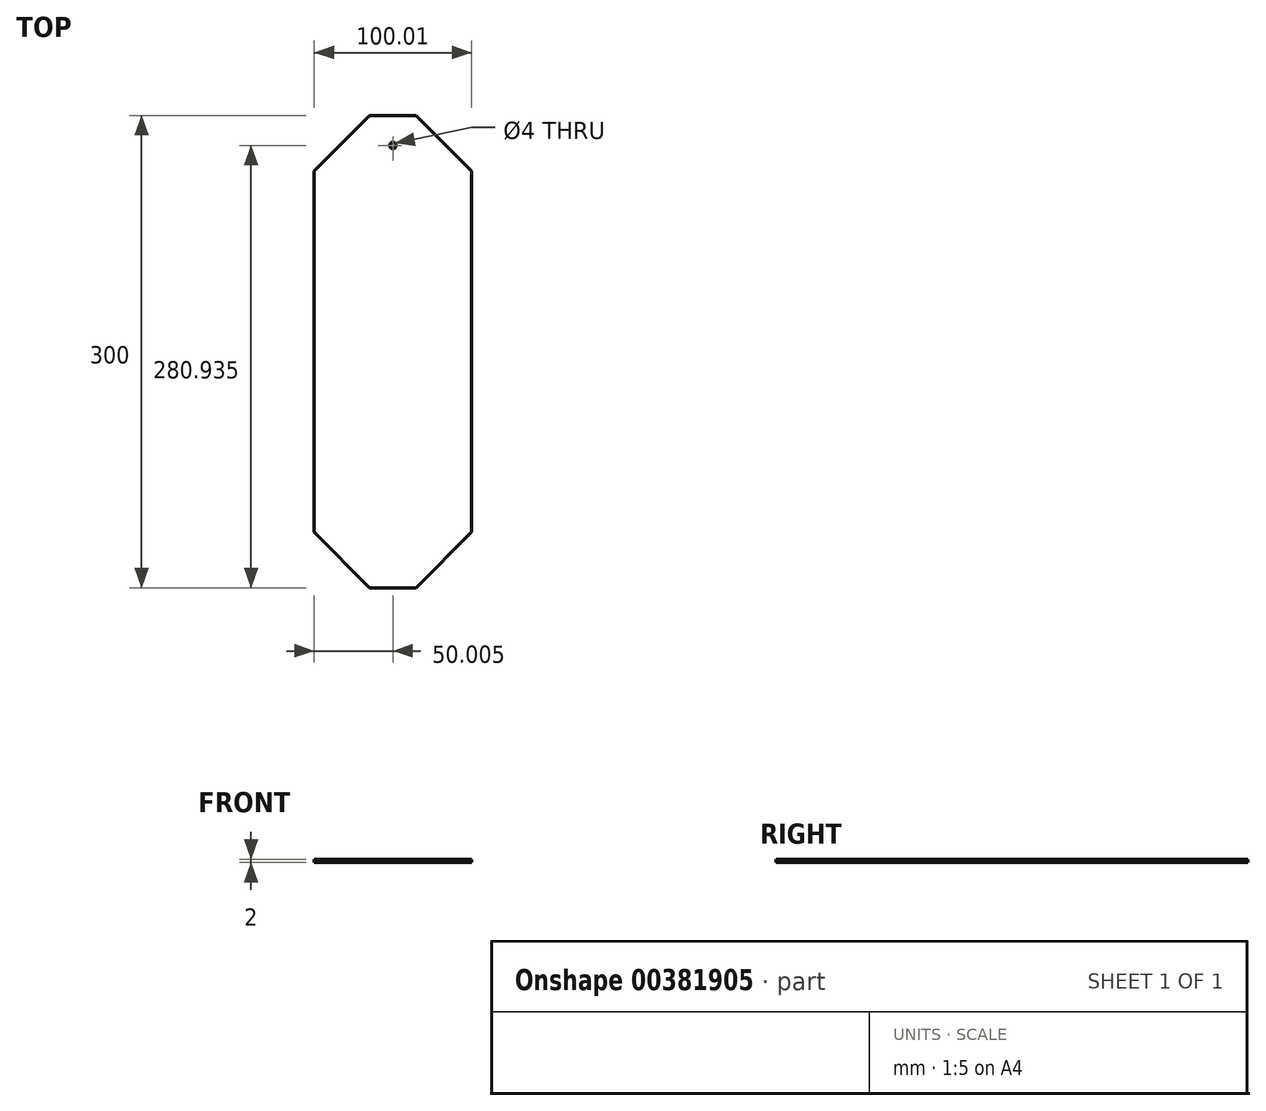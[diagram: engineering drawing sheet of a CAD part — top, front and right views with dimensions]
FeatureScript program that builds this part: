
annotation { "Feature Type Name" : "Feature", "Feature Type Description" : "" }
export const myFeature = defineFeature(function(context is Context, id is Id, definition is map)
    precondition{}
    {
        {
            var Q0;
            Q0=qCreatedBy(makeId("Top.planeOp"),FACE);
            var sketch = newSketch(context, id + "F0", { "sketchPlane" : qUnion([Q0])});
            skLineSegment(sketch, "E0", {"start": v(0, 0) * mm, "end": v(29.3, 0) * mm});
            skLineSegment(sketch, "E1", {"start": v(0, 0) * mm, "end": v(-35.35, 35.36) * mm});
            skLineSegment(sketch, "E2", {"start": v(-35.35, 35.36) * mm, "end": v(-35.35, 264.64) * mm});
            skLineSegment(sketch, "E3", {"start": v(-35.36, 264.64) * mm, "end": v(0, 300) * mm});
            skLineSegment(sketch, "E4", {"start": v(0, 300) * mm, "end": v(29.29, 300) * mm});
            skLineSegment(sketch, "E5", {"start": v(14.64, 300) * mm, "end": v(14.65, 0) * mm, "construction": true});
            skLineSegment(sketch, "E6.MirrorCS", {"start": v(64.65, 264.64) * mm, "end": v(29.3, 300) * mm});
            skLineSegment(sketch, "E7.MirrorCS", {"start": v(64.65, 35.36) * mm, "end": v(64.64, 264.64) * mm});
            skLineSegment(sketch, "E8.MirrorCS", {"start": v(29.3, 0) * mm, "end": v(64.65, 35.36) * mm});
            skCircle(sketch, "E9", {"center": v(14.65, 280.94) * mm, "radius": 2 * mm});
            skSolve(sketch);
        }
        {
            var Q0;
            Q0=makeQuery(id+"F0.imprint","IMPRINT",FACE,{"disambiguationData":[TD([[makeQuery(id+"F0.imprint","IMPRINT",EDGE,{"derivedFrom":sQuery(id+"F0.wireOp",EDGE,"E0")}),1.0]])]});
            extrude(context, id + "F1", {"entities" : qUnion([Q0]), "depth" : 2 * mm});
        }
    });
